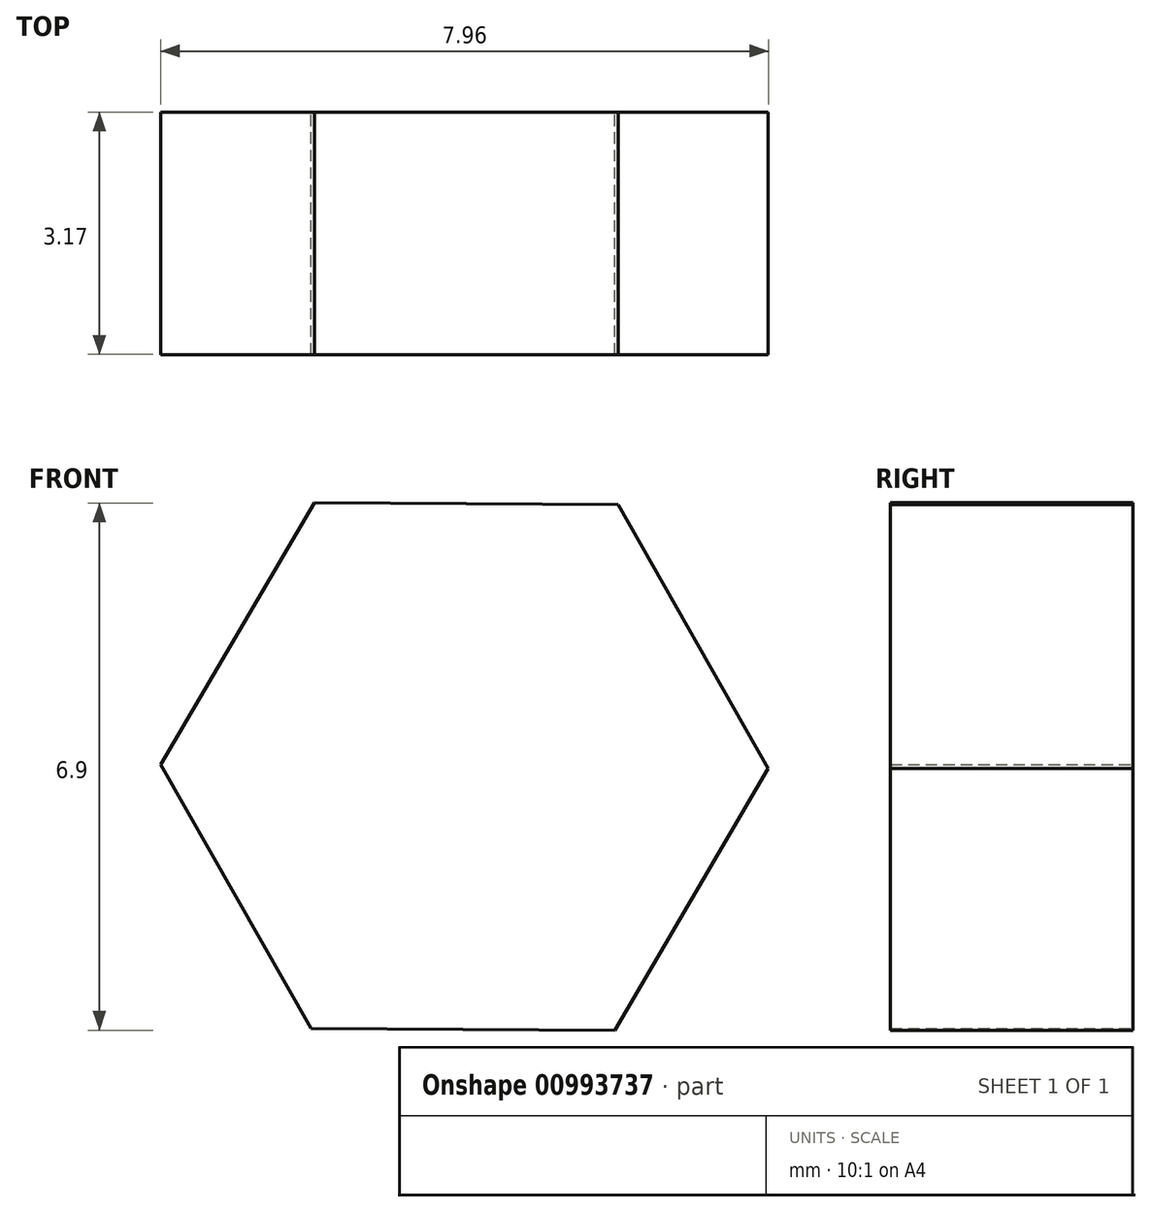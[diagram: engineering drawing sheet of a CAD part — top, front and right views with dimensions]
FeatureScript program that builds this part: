
annotation { "Feature Type Name" : "Feature", "Feature Type Description" : "" }
export const myFeature = defineFeature(function(context is Context, id is Id, definition is map)
    precondition{}
    {
        {
            var Q0;
            Q0=qCreatedBy(makeId("Front.planeOp"),FACE);
            var sketch = newSketch(context, id + "F0", { "sketchPlane" : qUnion([Q0])});
            skCircle(sketch, "E0.cCircle", {"center": v(0, 0) * mm, "radius": 3.44 * mm, "construction": true});
            skLineSegment(sketch, "E0.0", {"start": v(-2, -3.43) * mm, "end": v(-3.98, 0.02) * mm});
            skLineSegment(sketch, "E0.1", {"start": v(-3.98, 0.02) * mm, "end": v(-1.97, 3.45) * mm});
            skLineSegment(sketch, "E0.2", {"start": v(-1.97, 3.45) * mm, "end": v(2, 3.43) * mm});
            skLineSegment(sketch, "E0.3", {"start": v(2, 3.43) * mm, "end": v(3.98, -0.02) * mm});
            skLineSegment(sketch, "E0.4", {"start": v(3.98, -0.02) * mm, "end": v(1.97, -3.45) * mm});
            skLineSegment(sketch, "E0.5", {"start": v(1.97, -3.45) * mm, "end": v(-2, -3.43) * mm});
            skPoint(sketch, "E0.0.midPoint", {"position": v(-3, -1.7) * mm});
            skSolve(sketch);
        }
        {
            var Q0;
            Q0 = qSketchRegion(id + "F0", true);
            extrude(context, id + "F1", {"entities" : qUnion([Q0]), "depth" : 3.17 * mm, "offsetDistance" : 25.4 * mm});
        }
    });
